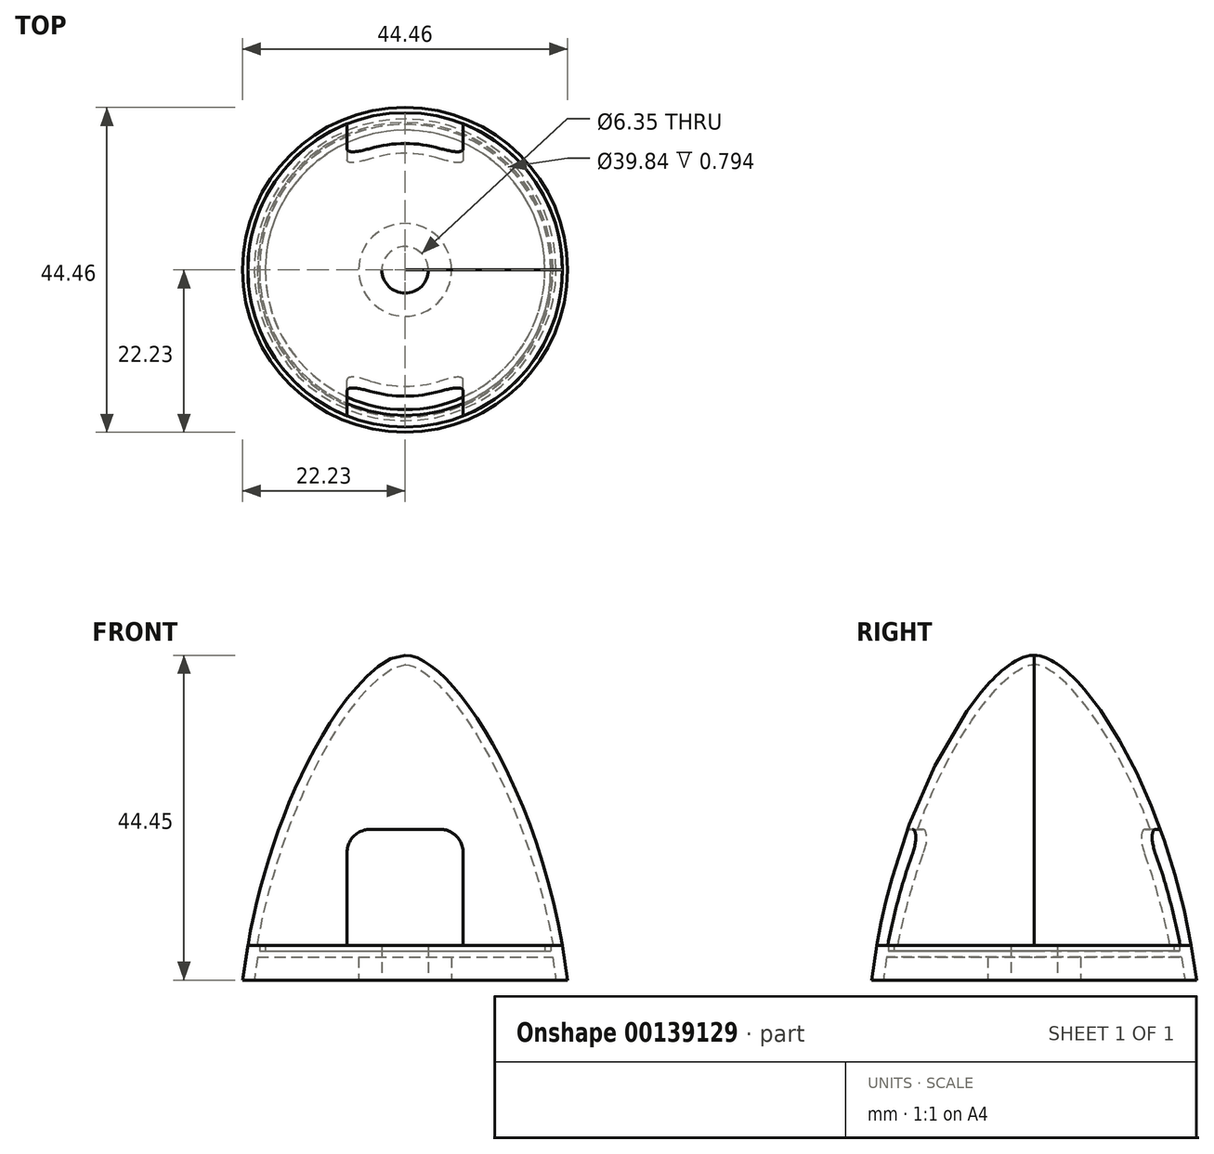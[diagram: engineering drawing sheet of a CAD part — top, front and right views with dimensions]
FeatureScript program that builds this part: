
annotation { "Feature Type Name" : "Feature", "Feature Type Description" : "" }
export const myFeature = defineFeature(function(context is Context, id is Id, definition is map)
    precondition{}
    {
        {
            var Q0;
            Q0=qCreatedBy(makeId("Front.planeOp"),FACE);
            var sketch = newSketch(context, id + "F0", { "sketchPlane" : qUnion([Q0])});
            skLineSegment(sketch, "E0", {"start": v(0, 0) * mm, "end": v(0, 44.45) * mm});
            skLineSegment(sketch, "E1", {"start": v(0, 0) * mm, "end": v(22.23, 0) * mm});
            skFitSpline(sketch, "E2", {"points": [v(0, 44.45) * mm, v(22.23, 0) * mm], "startDerivative": vector(19.05, 0) * mm, "endDerivative": vector(9.53, -76.2) * mm});
            skLineSegment(sketch, "E3", {"start": v(0, 4.76) * mm, "end": v(21.5, 4.76) * mm});
            skSolve(sketch);
        }
        {
            var Q0;
            Q0=qCreatedBy(makeId("Front.planeOp"),FACE);
            var sketch = newSketch(context, id + "F1", { "sketchPlane" : qUnion([Q0])});
            skLineSegment(sketch, "E4", {"start": v(3.17, 0) * mm, "end": v(3.17, 4.76) * mm});
            skLineSegment(sketch, "E5", {"start": v(3.18, 4.76) * mm, "end": v(19.13, 4.76) * mm});
            skLineSegment(sketch, "E6", {"start": v(19.13, 4.76) * mm, "end": v(19.13, 3.97) * mm});
            skLineSegment(sketch, "E7", {"start": v(19.13, 3.97) * mm, "end": v(19.92, 3.97) * mm});
            skLineSegment(sketch, "E8", {"start": v(19.92, 3.97) * mm, "end": v(19.92, 4.76) * mm});
            skLineSegment(sketch, "E9", {"start": v(19.92, 4.76) * mm, "end": v(21.5, 4.76) * mm});
            skLineSegment(sketch, "E10", {"start": v(21.5, 4.76) * mm, "end": v(22.22, 0) * mm});
            skLineSegment(sketch, "E11", {"start": v(22.23, 0) * mm, "end": v(20.64, 0) * mm});
            skLineSegment(sketch, "E12", {"start": v(6.35, 0) * mm, "end": v(3.18, 0) * mm});
            skLineSegment(sketch, "E13", {"start": v(6.35, 0) * mm, "end": v(6.35, 3.18) * mm});
            skLineSegment(sketch, "E14", {"start": v(6.35, 3.18) * mm, "end": v(20.16, 3.18) * mm});
            skLineSegment(sketch, "E15", {"start": v(20.16, 3.18) * mm, "end": v(20.64, 0) * mm});
            skSolve(sketch);
        }
        {
            var Q0;
            Q0=qCreatedBy(makeId("Front.planeOp"),FACE);
            var sketch = newSketch(context, id + "F2", { "sketchPlane" : qUnion([Q0])});
            skLineSegment(sketch, "E16", {"start": v(0, 4.76) * mm, "end": v(7.94, 4.76) * mm});
            skLineSegment(sketch, "E17", {"start": v(7.94, 4.76) * mm, "end": v(7.94, 17.46) * mm});
            skLineSegment(sketch, "E18", {"start": v(0, 20.64) * mm, "end": v(4.76, 20.64) * mm});
            skArc(sketch, "E19", {"start": v(7.94, 17.46) * mm, "mid": v(7, 19.7) * mm, "end": v(4.76, 20.64) * mm});
            skLineSegment(sketch, "E20", {"start": v(0, 0) * mm, "end": v(0, 20.64) * mm, "construction": true});
            skPoint(sketch, "E20.endSnap0", {"position": v(0, 4.76) * mm});
            skPoint(sketch, "E21.orphan", {"position": v(-7.94, 4.76) * mm});
            skLineSegment(sketch, "E22.MirrorCS", {"start": v(0, 20.64) * mm, "end": v(-4.76, 20.64) * mm});
            skArc(sketch, "E23.MirrorCS", {"start": v(-7.94, 17.46) * mm, "mid": v(-7, 19.7) * mm, "end": v(-4.76, 20.64) * mm});
            skLineSegment(sketch, "E24.MirrorCS", {"start": v(-7.94, 4.76) * mm, "end": v(-7.94, 17.46) * mm});
            skLineSegment(sketch, "E25.MirrorCS", {"start": v(0, 4.76) * mm, "end": v(-7.94, 4.76) * mm});
            skSolve(sketch);
        }
        {
            var Q0;
            {var subQ3=sQuery(id+"F0.wireOp",EDGE,"E3");Q0=makeQuery(id+"F0.imprint","IMPRINT",FACE,{"disambiguationData":[TD([[makeQuery(id+"F0.imprint","IMPRINT",EDGE,{"derivedFrom":subQ3}),1.0]])]});}
            var Q1;
            Q1=sQuery(id+"F0.wireOp",EDGE,"E0");
            revolve(context, id + "F3", {"entities" : qUnion([Q0]), "axis" : qUnion([Q1]), "revolveType" : RevolveType.FULL});
        }
        {
            var Q0;
            Q0=makeQuery(id+"F3.opRevolve","SWEPT_FACE",FACE,{"disambiguationData":[OSD([sQuery(id+"F0.wireOp",EDGE,"E3")])]});
            shell(context, id + "F4", {"entities" : qUnion([Q0]), "thickness" : 1.27 * mm});
        }
        {
            var Q0;
            Q0=makeQuery(id+"F1.imprint","IMPRINT",FACE,{"disambiguationData":[TD([[makeQuery(id+"F1.imprint","IMPRINT",EDGE,{"derivedFrom":sQuery(id+"F1.wireOp",EDGE,"E4")}),-1.0]])]});
            var Q1;
            Q1=sQuery(id+"F0.wireOp",EDGE,"E0");
            revolve(context, id + "F5", {"entities" : qUnion([Q0]), "axis" : qUnion([Q1]), "revolveType" : RevolveType.FULL});
        }
        {
            var Q0;
            {var subQ0=sQuery(id+"F2.wireOp",EDGE,"7cef10a8-6575-4cf5-b21a-28d51c7f3ad50.MirrorCS");Q0=makeQuery(id+"F2.imprint","IMPRINT",FACE,{"disambiguationData":[TD([[makeQuery(id+"F2.imprint","IMPRINT",EDGE,{"derivedFrom":subQ0}),-1.0]])]});}
            var Q1;
            {var subQ0=sQuery(id+"F2.wireOp",EDGE,"E17");Q1=makeQuery(id+"F2.imprint","IMPRINT",FACE,{"disambiguationData":[TD([[makeQuery(id+"F2.imprint","IMPRINT",EDGE,{"derivedFrom":subQ0}),1.0]])]});}
            var Q2;
            Q2=makeQuery(id+"F3.opRevolve","SWEPT_BODY",BODY,{"disambiguationData":[OSD([sQuery(id+"F0.wireOp",EDGE,"E0"),sQuery(id+"F0.wireOp",EDGE,"E2"),sQuery(id+"F0.wireOp",EDGE,"E3")])]});
            extrude(context, id + "F6", {"entities" : qUnion([Q0, Q1]), "operationType" : NewBodyOperationType.REMOVE, "endBound" : BoundingType.THROUGH_ALL, "endBoundEntityBody" : qUnion([Q2]), "depth" : 25.4 * mm});
        }
        {
            var Q0;
            Q0=makeQuery(id+"F2.imprint","IMPRINT",FACE,{"disambiguationData":[TD([[makeQuery(id+"F2.imprint","IMPRINT",EDGE,{"derivedFrom":sQuery(id+"F2.wireOp",EDGE,"E16")}),1.0]])]});
            var Q1;
            Q1=makeQuery(id+"F3.opRevolve","SWEPT_BODY",BODY,{"disambiguationData":[OSD([sQuery(id+"F0.wireOp",EDGE,"E0"),sQuery(id+"F0.wireOp",EDGE,"E2"),sQuery(id+"F0.wireOp",EDGE,"E3")])]});
            extrude(context, id + "F7", {"entities" : qUnion([Q0]), "operationType" : NewBodyOperationType.REMOVE, "endBound" : BoundingType.THROUGH_ALL, "oppositeDirection" : true, "endBoundEntityBody" : qUnion([Q1]), "depth" : 25.4 * mm});
        }
    });
